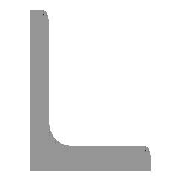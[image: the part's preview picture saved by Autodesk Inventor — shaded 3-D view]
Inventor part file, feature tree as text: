
AUTODESK INVENTOR PART (.ipt)
format: ipt  version: 2017 (Build 210142000, 142)  size: 120,832 bytes
history: native  units: mm (DEFAULTED — no unit token found)
features: other x4, sketch x2, plane x1
ambient origin geometry x8: Origin, YZ Plane, XZ Plane, XY Plane, X Axis, Y Axis, Z Axis, Center Point
bodies: Solid1 (feature_tree), Body (feature_tree)
feature tree (7):
  parser-record x1  (decoder bookkeeping rows leaked as tree rows — omitted from the tree; the rows remain in map.json)
  other  "Driven Length"
  other  "Start plane"
  other  "End plane"
  sketch  "Sketch3"  dims[d0=63.5mm]
  plane  "Work Plane3"
  sketch  "Sketch4"  dims[d1=63.5mm d2=6.35mm d3=6.35mm d4=1155.7mm d5=0.0mm d10=0.0mm d11=0.0mm d12=641.35mm d13=1797.05mm d14=7.874mm d15=3.81mm d16=90.0deg d17=1155.7mm]
